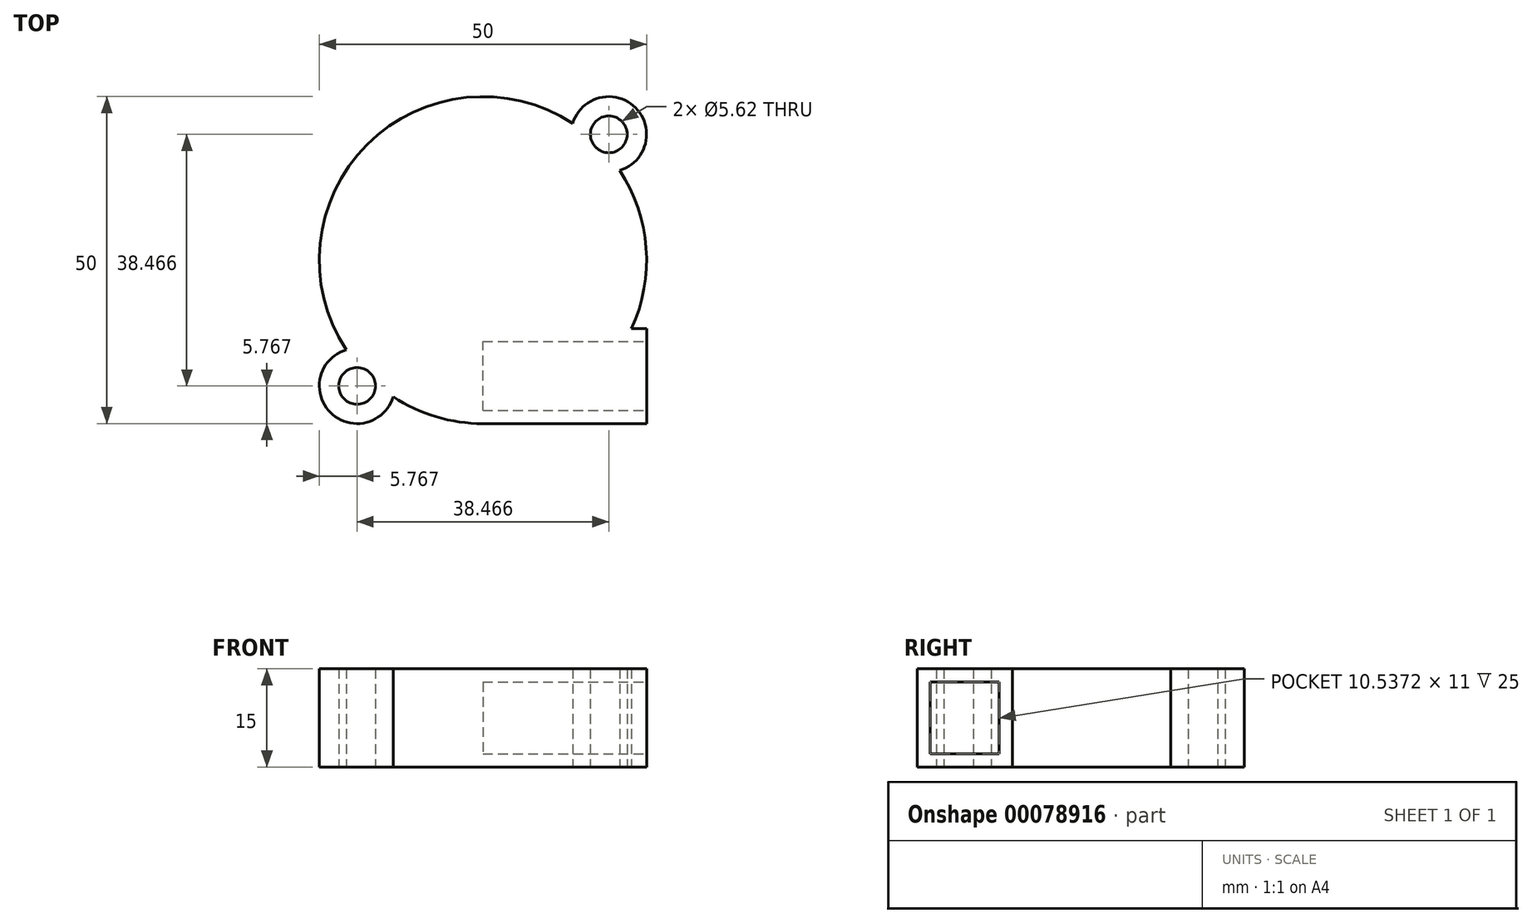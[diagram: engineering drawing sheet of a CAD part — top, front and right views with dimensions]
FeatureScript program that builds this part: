
annotation { "Feature Type Name" : "Feature", "Feature Type Description" : "" }
export const myFeature = defineFeature(function(context is Context, id is Id, definition is map)
    precondition{}
    {
        {
            var Q0;
            Q0=qCreatedBy(makeId("Top.planeOp"),FACE);
            var sketch = newSketch(context, id + "F0", { "sketchPlane" : qUnion([Q0])});
            skLineSegment(sketch, "E0.bottom", {"start": v(25, 0) * mm, "end": v(50, 0) * mm});
            skLineSegment(sketch, "E0.right", {"start": v(50, 0) * mm, "end": v(50, 14.54) * mm});
            skLineSegment(sketch, "E1", {"start": v(25, 50) * mm, "end": v(25, 0) * mm, "construction": true});
            skCircle(sketch, "E2", {"center": v(44.23, 44.23) * mm, "radius": 2.8 * mm});
            skLineSegment(sketch, "E3", {"start": v(0, 50) * mm, "end": v(50, 0) * mm, "construction": true});
            skCircle(sketch, "E4.MirrorC", {"center": v(5.77, 5.77) * mm, "radius": 2.8 * mm});
            skArc(sketch, "E5", {"start": v(38.71, 45.9) * mm, "mid": v(7.32, 42.68) * mm, "end": v(4.1, 11.29) * mm});
            skArc(sketch, "E6", {"start": v(45.9, 38.71) * mm, "mid": v(48.31, 48.31) * mm, "end": v(38.71, 45.9) * mm});
            skArc(sketch, "E7.MirrorCS", {"start": v(11.29, 4.1) * mm, "mid": v(1.69, 1.69) * mm, "end": v(4.1, 11.29) * mm});
            skArc(sketch, "E8.trimOffspring", {"start": v(11.29, 4.1) * mm, "mid": v(42.68, 7.32) * mm, "end": v(45.9, 38.71) * mm});
            skPoint(sketch, "E9.orphan", {"position": v(0, 0) * mm});
            skPoint(sketch, "E10.orphan", {"position": v(50, 50) * mm});
            skLineSegment(sketch, "E11", {"start": v(50, 14.54) * mm, "end": v(47.7, 14.54) * mm});
            skSolve(sketch);
        }
        {
            var Q0;
            Q0 = qSketchRegion(id + "F0", true);
            extrude(context, id + "F1", {"entities" : qUnion([Q0]), "depth" : 15 * mm});
        }
        {
            var Q0;
            Q0=makeQuery(id+"F1.opExtrude","SWEPT_FACE",FACE,{"disambiguationData":[OSD([sQuery(id+"F0.wireOp",EDGE,"E0.right")])]});
            var sketch = newSketch(context, id + "F2", { "sketchPlane" : qUnion([Q0])});
            skLineSegment(sketch, "E12.0", {"start": v(2, 2) * mm, "end": v(12.54, 2) * mm});
            skLineSegment(sketch, "E12.1", {"start": v(2, 13) * mm, "end": v(2, 2) * mm});
            skLineSegment(sketch, "E12.2", {"start": v(12.54, 13) * mm, "end": v(2, 13) * mm});
            skLineSegment(sketch, "E12.3", {"start": v(12.54, 2) * mm, "end": v(12.54, 13) * mm});
            skSolve(sketch);
        }
        {
            var Q0;
            Q0 = qSketchRegion(id + "F2", true);
            extrude(context, id + "F3", {"entities" : qUnion([Q0]), "operationType" : NewBodyOperationType.REMOVE, "oppositeDirection" : true, "depth" : 25 * mm});
        }
    });
